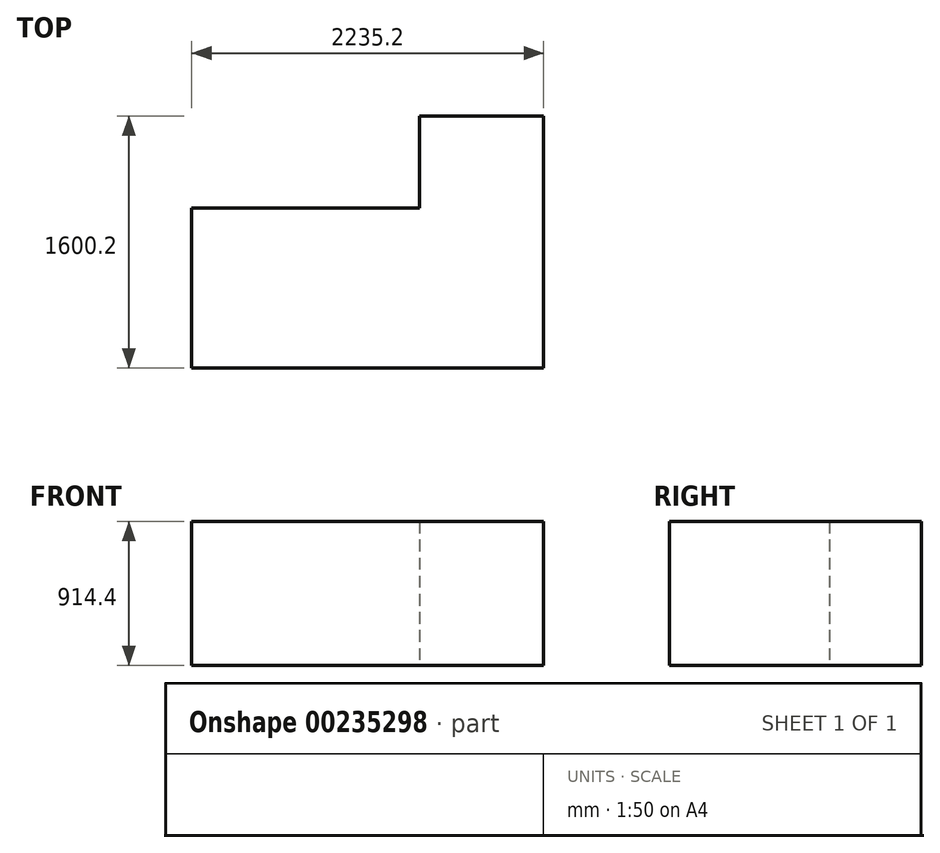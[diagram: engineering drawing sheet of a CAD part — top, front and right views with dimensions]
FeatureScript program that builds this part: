
annotation { "Feature Type Name" : "Feature", "Feature Type Description" : "" }
export const myFeature = defineFeature(function(context is Context, id is Id, definition is map)
    precondition{}
    {
        {
            var Q0;
            Q0=qCreatedBy(makeId("Top.planeOp"),FACE);
            var sketch = newSketch(context, id + "F0", { "sketchPlane" : qUnion([Q0])});
            skLineSegment(sketch, "E0", {"start": v(-1447.8, 0) * mm, "end": v(-1447.8, -1016) * mm});
            skLineSegment(sketch, "E1", {"start": v(-1447.8, -1016) * mm, "end": v(787.4, -1016) * mm});
            skLineSegment(sketch, "E2", {"start": v(787.4, -1016) * mm, "end": v(787.4, 584.2) * mm});
            skLineSegment(sketch, "E3", {"start": v(787.4, 584.2) * mm, "end": v(0, 584.2) * mm});
            skLineSegment(sketch, "E4", {"start": v(0, 584.2) * mm, "end": v(0, 0) * mm});
            skLineSegment(sketch, "E5", {"start": v(0, 0) * mm, "end": v(-1447.8, 0) * mm});
            skSolve(sketch);
        }
        {
            var Q0;
            Q0=makeQuery(id+"F0.imprint","IMPRINT",FACE,{"disambiguationData":[TD([[makeQuery(id+"F0.imprint","IMPRINT",EDGE,{"derivedFrom":sQuery(id+"F0.wireOp",EDGE,"E0")}),1.0]])]});
            extrude(context, id + "F1", {"entities" : qUnion([Q0]), "depth" : 914.4 * mm});
        }
    });
